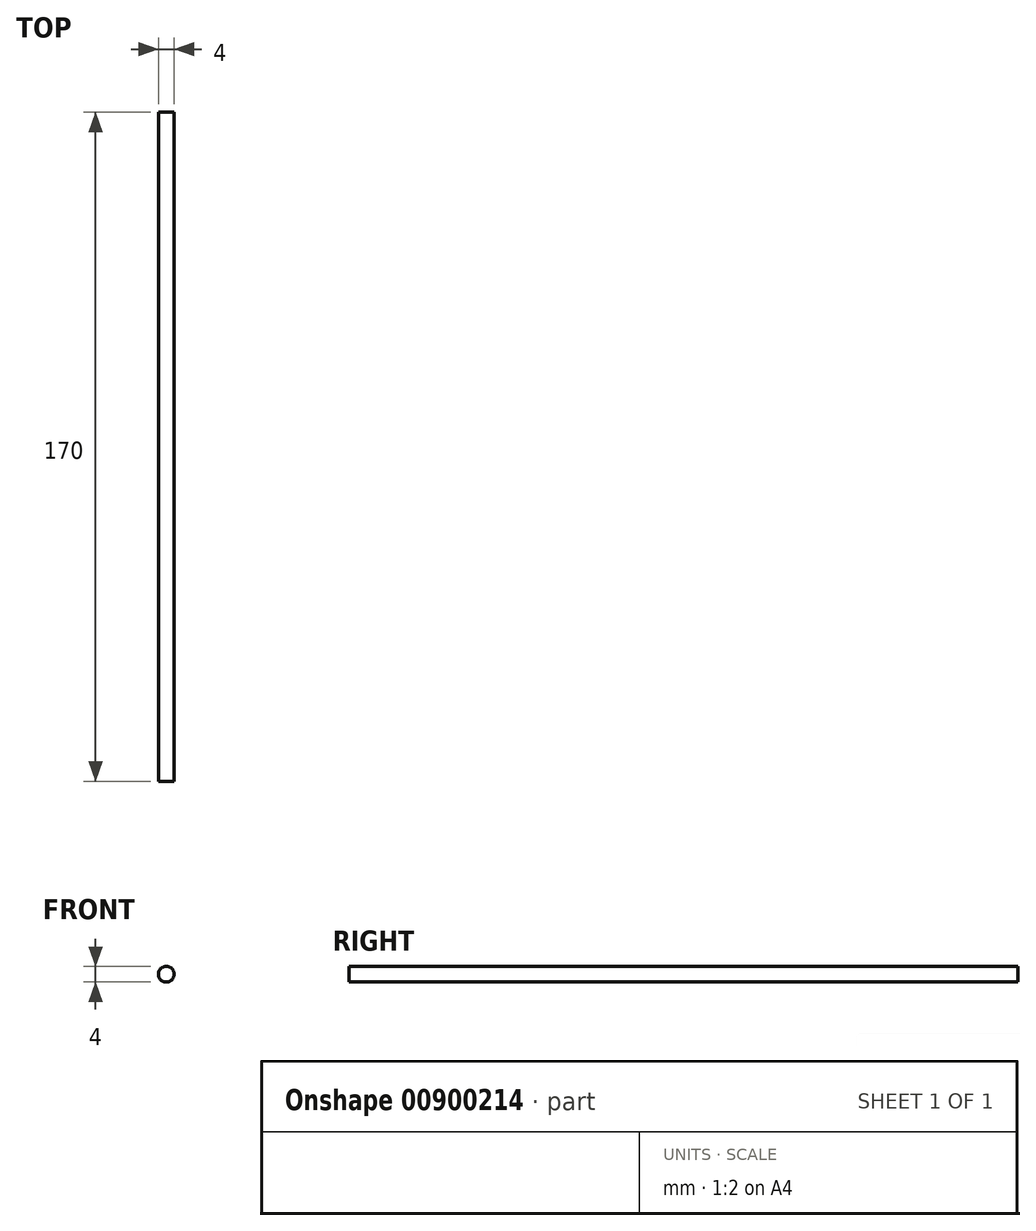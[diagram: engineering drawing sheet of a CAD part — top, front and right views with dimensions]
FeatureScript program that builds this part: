
annotation { "Feature Type Name" : "Feature", "Feature Type Description" : "" }
export const myFeature = defineFeature(function(context is Context, id is Id, definition is map)
    precondition{}
    {
        {
            var Q0;
            Q0=qCreatedBy(makeId("Front.planeOp"),FACE);
            var sketch = newSketch(context, id + "F0", { "sketchPlane" : qUnion([Q0])});
            skCircle(sketch, "E0", {"center": v(0, 0) * mm, "radius": 2 * mm});
            skSolve(sketch);
        }
        {
            var Q0;
            Q0=makeQuery(id+"F0.imprint","IMPRINT",FACE,{"disambiguationData":[TD([[makeQuery(id+"F0.imprint","IMPRINT",EDGE,{"derivedFrom":sQuery(id+"F0.wireOp",EDGE,"E0")}),1.0]])]});
            extrude(context, id + "F1", {"entities" : qUnion([Q0]), "endBound" : BoundingType.SYMMETRIC, "depth" : 170 * mm, "offsetDistance" : 25 * mm});
        }
    });
